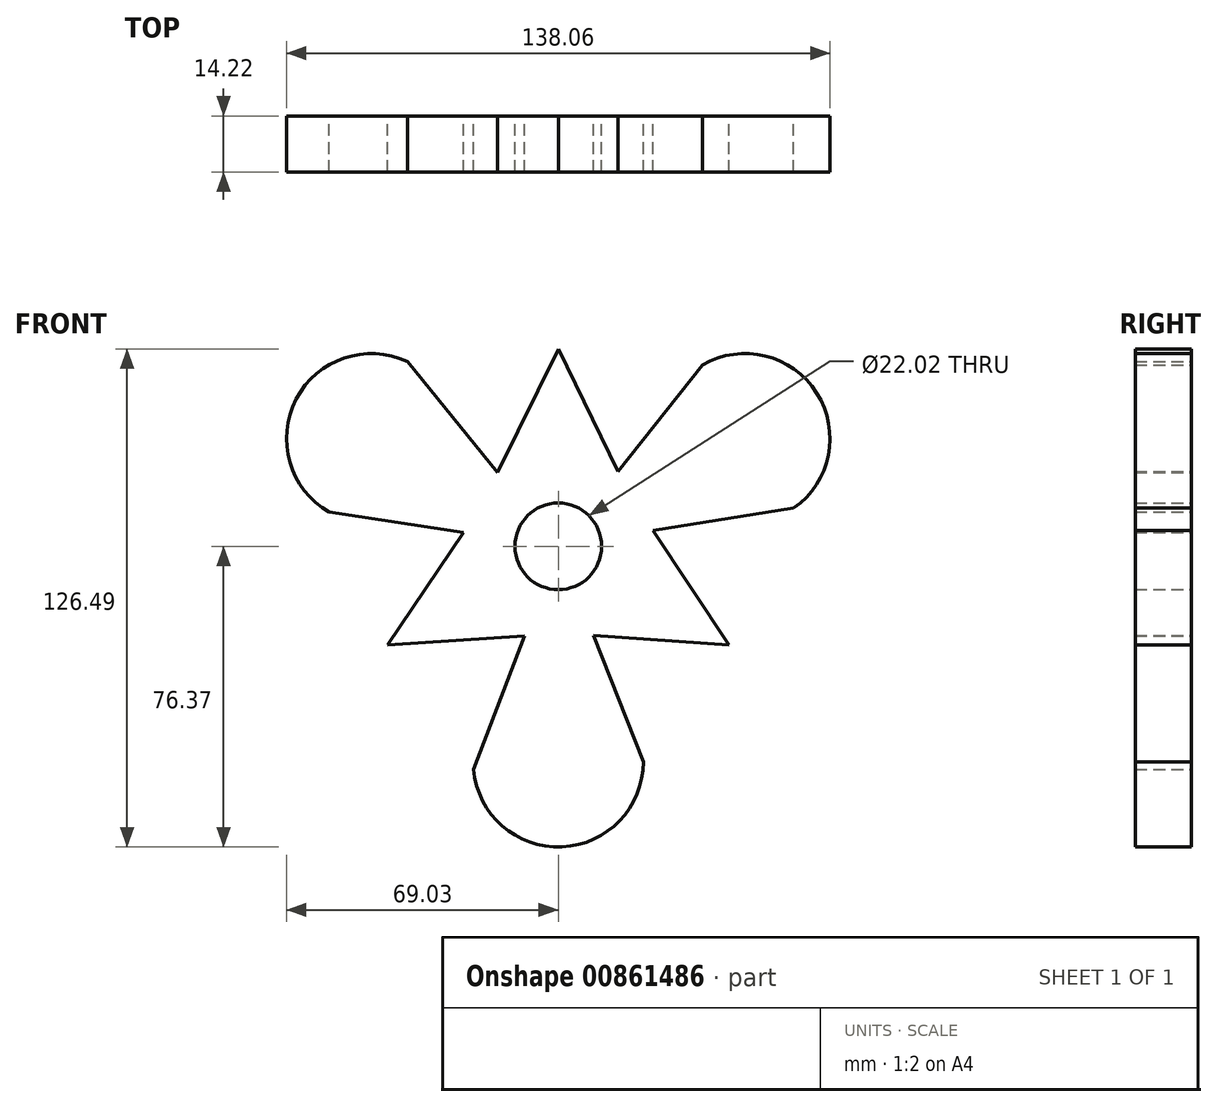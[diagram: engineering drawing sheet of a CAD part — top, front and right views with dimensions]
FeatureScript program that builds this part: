
annotation { "Feature Type Name" : "Feature", "Feature Type Description" : "" }
export const myFeature = defineFeature(function(context is Context, id is Id, definition is map)
    precondition{}
    {
        {
            var Q0;
            Q0=qCreatedBy(makeId("Front.planeOp"),FACE);
            var sketch = newSketch(context, id + "F0", { "sketchPlane" : qUnion([Q0])});
            skCircle(sketch, "E0", {"center": v(0, 0) * mm, "radius": 24.33 * mm});
            skLineSegment(sketch, "E1", {"start": v(0, 0) * mm, "end": v(0, -54.77) * mm});
            skArc(sketch, "E2", {"start": v(-21.51, -56.63) * mm, "mid": v(0.93, -76.35) * mm, "end": v(21.6, -54.77) * mm});
            skLineSegment(sketch, "E3", {"start": v(-21.51, -56.63) * mm, "end": v(-8.54, -22.79) * mm});
            skLineSegment(sketch, "E4", {"start": v(21.6, -54.77) * mm, "end": v(8.94, -22.63) * mm});
            skLineSegment(sketch, "E5", {"start": v(-8.54, -22.79) * mm, "end": v(0, 0) * mm});
            skLineSegment(sketch, "E6", {"start": v(8.94, -22.63) * mm, "end": v(0, 0) * mm});
            skArc(sketch, "E7.1.0", {"start": v(59.8, 9.69) * mm, "mid": v(65.65, 38.98) * mm, "end": v(36.64, 46.09) * mm});
            skLineSegment(sketch, "E7.1.1", {"start": v(59.8, 9.69) * mm, "end": v(24, 4) * mm});
            skLineSegment(sketch, "E7.1.2", {"start": v(36.64, 46.09) * mm, "end": v(15.13, 19.06) * mm});
            skLineSegment(sketch, "E7.1.3", {"start": v(15.13, 19.06) * mm, "end": v(0, 0) * mm});
            skLineSegment(sketch, "E7.1.4", {"start": v(24, 4) * mm, "end": v(0, 0) * mm});
            skLineSegment(sketch, "E7.1.5", {"start": v(0, 0) * mm, "end": v(47.44, 27.39) * mm});
            skArc(sketch, "E7.2.0", {"start": v(-38.3, 46.95) * mm, "mid": v(-66.59, 37.37) * mm, "end": v(-58.23, 8.69) * mm});
            skLineSegment(sketch, "E7.2.1", {"start": v(-38.3, 46.95) * mm, "end": v(-15.47, 18.79) * mm});
            skLineSegment(sketch, "E7.2.2", {"start": v(-58.23, 8.69) * mm, "end": v(-24.07, 3.58) * mm});
            skLineSegment(sketch, "E7.2.3", {"start": v(-24.07, 3.58) * mm, "end": v(0, 0) * mm});
            skLineSegment(sketch, "E7.2.4", {"start": v(-15.47, 18.79) * mm, "end": v(0, 0) * mm});
            skLineSegment(sketch, "E7.2.5", {"start": v(0, 0) * mm, "end": v(-47.44, 27.39) * mm});
            skLineSegment(sketch, "E8", {"start": v(8.94, -22.63) * mm, "end": v(43.4, -25.06) * mm});
            skLineSegment(sketch, "E9", {"start": v(24, 4) * mm, "end": v(43.4, -25.06) * mm});
            skLineSegment(sketch, "E10.1.0", {"start": v(15.13, 19.06) * mm, "end": v(0, 50.12) * mm});
            skLineSegment(sketch, "E10.1.1", {"start": v(-15.47, 18.79) * mm, "end": v(0, 50.12) * mm});
            skLineSegment(sketch, "E10.2.0", {"start": v(-24.07, 3.58) * mm, "end": v(-43.4, -25.06) * mm});
            skLineSegment(sketch, "E10.2.1", {"start": v(-8.54, -22.79) * mm, "end": v(-43.4, -25.06) * mm});
            skSolve(sketch);
        }
        {
            var Q0;
            Q0=qCreatedBy(makeId("Front.planeOp"),FACE);
            var sketch = newSketch(context, id + "F1", { "sketchPlane" : qUnion([Q0])});
            skCircle(sketch, "E11", {"center": v(0, 0) * mm, "radius": 11.06 * mm});
            skSolve(sketch);
        }
        {
            var Q0;
            Q0=makeQuery(id+"F0.imprint","IMPRINT",FACE,{"disambiguationData":[TD([[makeQuery(id+"F0.imprint","IMPRINT",EDGE,{"derivedFrom":sQuery(id+"F0.wireOp",EDGE,"E7.1.0")}),1.0]])]});
            var Q1;
            {var subQ0=sQuery(id+"F0.wireOp",EDGE,"E8");Q1=makeQuery(id+"F0.imprint","IMPRINT",FACE,{"disambiguationData":[TD([[makeQuery(id+"F0.imprint","IMPRINT",EDGE,{"derivedFrom":subQ0}),1.0]])]});}
            var Q2;
            {var subQ0=sQuery(id+"F0.wireOp",EDGE,"E6");Q2=makeQuery(id+"F0.imprint","IMPRINT",FACE,{"disambiguationData":[TD([[makeQuery(id+"F0.imprint","IMPRINT",EDGE,{"derivedFrom":subQ0}),-1.0]])]});}
            var Q3;
            {var subQ0=sQuery(id+"F0.wireOp",EDGE,"E7.1.3");Q3=makeQuery(id+"F0.imprint","IMPRINT",FACE,{"disambiguationData":[TD([[makeQuery(id+"F0.imprint","IMPRINT",EDGE,{"derivedFrom":subQ0}),-1.0]])]});}
            var Q4;
            {var subQ0=sQuery(id+"F0.wireOp",EDGE,"E7.2.3");Q4=makeQuery(id+"F0.imprint","IMPRINT",FACE,{"disambiguationData":[TD([[makeQuery(id+"F0.imprint","IMPRINT",EDGE,{"derivedFrom":subQ0}),1.0]])]});}
            var Q5;
            {var subQ0=sQuery(id+"F0.wireOp",EDGE,"E7.2.4");Q5=makeQuery(id+"F0.imprint","IMPRINT",FACE,{"disambiguationData":[TD([[makeQuery(id+"F0.imprint","IMPRINT",EDGE,{"derivedFrom":subQ0}),-1.0]])]});}
            var Q6;
            {var subQ0=sQuery(id+"F0.wireOp",EDGE,"E6");Q6=makeQuery(id+"F0.imprint","IMPRINT",FACE,{"disambiguationData":[TD([[makeQuery(id+"F0.imprint","IMPRINT",EDGE,{"derivedFrom":subQ0}),1.0]])]});}
            var Q7;
            {var subQ0=sQuery(id+"F0.wireOp",EDGE,"E7.1.4");Q7=makeQuery(id+"F0.imprint","IMPRINT",FACE,{"disambiguationData":[TD([[makeQuery(id+"F0.imprint","IMPRINT",EDGE,{"derivedFrom":subQ0}),-1.0]])]});}
            var Q8;
            Q8=makeQuery(id+"F0.imprint","IMPRINT",FACE,{"disambiguationData":[TD([[makeQuery(id+"F0.imprint","IMPRINT",EDGE,{"derivedFrom":sQuery(id+"F0.wireOp",EDGE,"E2")}),1.0]])]});
            var Q9;
            Q9=makeQuery(id+"F0.imprint","IMPRINT",FACE,{"disambiguationData":[TD([[makeQuery(id+"F0.imprint","IMPRINT",EDGE,{"derivedFrom":sQuery(id+"F0.wireOp",EDGE,"E7.2.0")}),1.0]])]});
            var Q10;
            {var subQ0=sQuery(id+"F0.wireOp",EDGE,"E10.1.0");Q10=makeQuery(id+"F0.imprint","IMPRINT",FACE,{"disambiguationData":[TD([[makeQuery(id+"F0.imprint","IMPRINT",EDGE,{"derivedFrom":subQ0}),1.0]])]});}
            var Q11;
            {var subQ0=sQuery(id+"F0.wireOp",EDGE,"E5");Q11=makeQuery(id+"F0.imprint","IMPRINT",FACE,{"disambiguationData":[TD([[makeQuery(id+"F0.imprint","IMPRINT",EDGE,{"derivedFrom":subQ0}),-1.0]])]});}
            var Q12;
            {var subQ0=sQuery(id+"F0.wireOp",EDGE,"E7.1.3");Q12=makeQuery(id+"F0.imprint","IMPRINT",FACE,{"disambiguationData":[TD([[makeQuery(id+"F0.imprint","IMPRINT",EDGE,{"derivedFrom":subQ0}),1.0]])]});}
            var Q13;
            {var subQ0=sQuery(id+"F0.wireOp",EDGE,"E5");Q13=makeQuery(id+"F0.imprint","IMPRINT",FACE,{"disambiguationData":[TD([[makeQuery(id+"F0.imprint","IMPRINT",EDGE,{"derivedFrom":subQ0}),1.0]])]});}
            var Q14;
            {var subQ2=sQuery(id+"F0.wireOp",EDGE,"E10.2.0");Q14=makeQuery(id+"F0.imprint","IMPRINT",FACE,{"disambiguationData":[TD([[makeQuery(id+"F0.imprint","IMPRINT",EDGE,{"derivedFrom":subQ2}),1.0]])]});}
            var Q15;
            Q15=sQuery(id+"F1.wireOp",EDGE,"E11");
            var Q16;
            Q16=sQuery(id+"F0.wireOp",EDGE,"E7.1.2");
            var Q17;
            Q17=sQuery(id+"F0.wireOp",EDGE,"E7.1.0");
            var Q18;
            Q18=sQuery(id+"F0.wireOp",EDGE,"E7.1.1");
            var Q19;
            Q19=sQuery(id+"F0.wireOp",EDGE,"E9");
            var Q20;
            Q20=sQuery(id+"F0.wireOp",EDGE,"E8");
            var Q21;
            Q21=sQuery(id+"F0.wireOp",EDGE,"E4");
            var Q22;
            Q22=sQuery(id+"F0.wireOp",EDGE,"E2");
            var Q23;
            Q23=sQuery(id+"F0.wireOp",EDGE,"E3");
            var Q24;
            Q24=sQuery(id+"F0.wireOp",EDGE,"E10.2.1");
            var Q25;
            Q25=sQuery(id+"F0.wireOp",EDGE,"E10.2.0");
            var Q26;
            Q26=sQuery(id+"F0.wireOp",EDGE,"E7.2.2");
            var Q27;
            Q27=sQuery(id+"F0.wireOp",EDGE,"E7.2.1");
            var Q28;
            Q28=sQuery(id+"F0.wireOp",EDGE,"E10.1.1");
            var Q29;
            Q29=sQuery(id+"F0.wireOp",EDGE,"E7.2.0");
            var Q30;
            Q30=sQuery(id+"F0.wireOp",EDGE,"E10.1.0");
            extrude(context, id + "F2", {"entities" : qUnion([Q0, Q1, Q2, Q3, Q4, Q5, Q6, Q7, Q8, Q9, Q10, Q11, Q12, Q13, Q14]), "surfaceEntities" : qUnion([Q15, Q16, Q17, Q18, Q19, Q20, Q21, Q22, Q23, Q24, Q25, Q26, Q27, Q28, Q29, Q30]), "depth" : 14.22 * mm, "offsetDistance" : 25.4 * mm});
        }
        {
            var Q0;
            Q0=makeQuery(id+"F2.opExtrude","CAP_FACE",FACE,{"disambiguationData":[OSD([sQuery(id+"F0.wireOp",EDGE,"E2"),sQuery(id+"F0.wireOp",EDGE,"E3"),sQuery(id+"F0.wireOp",EDGE,"E4"),sQuery(id+"F0.wireOp",EDGE,"E7.1.0"),sQuery(id+"F0.wireOp",EDGE,"E7.1.1"),sQuery(id+"F0.wireOp",EDGE,"E7.1.2"),sQuery(id+"F0.wireOp",EDGE,"E7.2.0"),sQuery(id+"F0.wireOp",EDGE,"E7.2.1"),sQuery(id+"F0.wireOp",EDGE,"E7.2.2"),sQuery(id+"F0.wireOp",EDGE,"E8"),sQuery(id+"F0.wireOp",EDGE,"E9"),sQuery(id+"F0.wireOp",EDGE,"E10.1.0"),sQuery(id+"F0.wireOp",EDGE,"E10.1.1"),sQuery(id+"F0.wireOp",EDGE,"E10.2.0"),sQuery(id+"F0.wireOp",EDGE,"E10.2.1")])],"isStart":true});
            var sketch = newSketch(context, id + "F3", { "sketchPlane" : qUnion([Q0])});
            skCircle(sketch, "E12", {"center": v(0, 0) * mm, "radius": 11.03 * mm});
            skSolve(sketch);
        }
        {
            var Q0;
            Q0=sQuery(id+"F3.wireOp",VERTEX,"E12.center");
            var Q1;
            Q1=makeQuery(id+"F2.opExtrude","SWEPT_BODY",BODY,{"disambiguationData":[OSD([sQuery(id+"F0.wireOp",EDGE,"E2"),sQuery(id+"F0.wireOp",EDGE,"E3"),sQuery(id+"F0.wireOp",EDGE,"E4"),sQuery(id+"F0.wireOp",EDGE,"E7.1.0"),sQuery(id+"F0.wireOp",EDGE,"E7.1.1"),sQuery(id+"F0.wireOp",EDGE,"E7.1.2"),sQuery(id+"F0.wireOp",EDGE,"E7.2.0"),sQuery(id+"F0.wireOp",EDGE,"E7.2.1"),sQuery(id+"F0.wireOp",EDGE,"E7.2.2"),sQuery(id+"F0.wireOp",EDGE,"E8"),sQuery(id+"F0.wireOp",EDGE,"E9"),sQuery(id+"F0.wireOp",EDGE,"E10.1.0"),sQuery(id+"F0.wireOp",EDGE,"E10.1.1"),sQuery(id+"F0.wireOp",EDGE,"E10.2.0"),sQuery(id+"F0.wireOp",EDGE,"E10.2.1")])]});
            hole(context, id + "F4", {"style" : HoleStyle.SIMPLE, "endStyle" : HoleEndStyle.THROUGH, "holeDiameter" : 22.02 * mm, "majorDiameter" : 6.35 * mm, "isTappedThrough" : true, "tappedDepth" : 12.7 * mm, "tapClearance" : 3, "locations" : qUnion([Q0]), "scope" : qUnion([Q1])});
        }
    });
